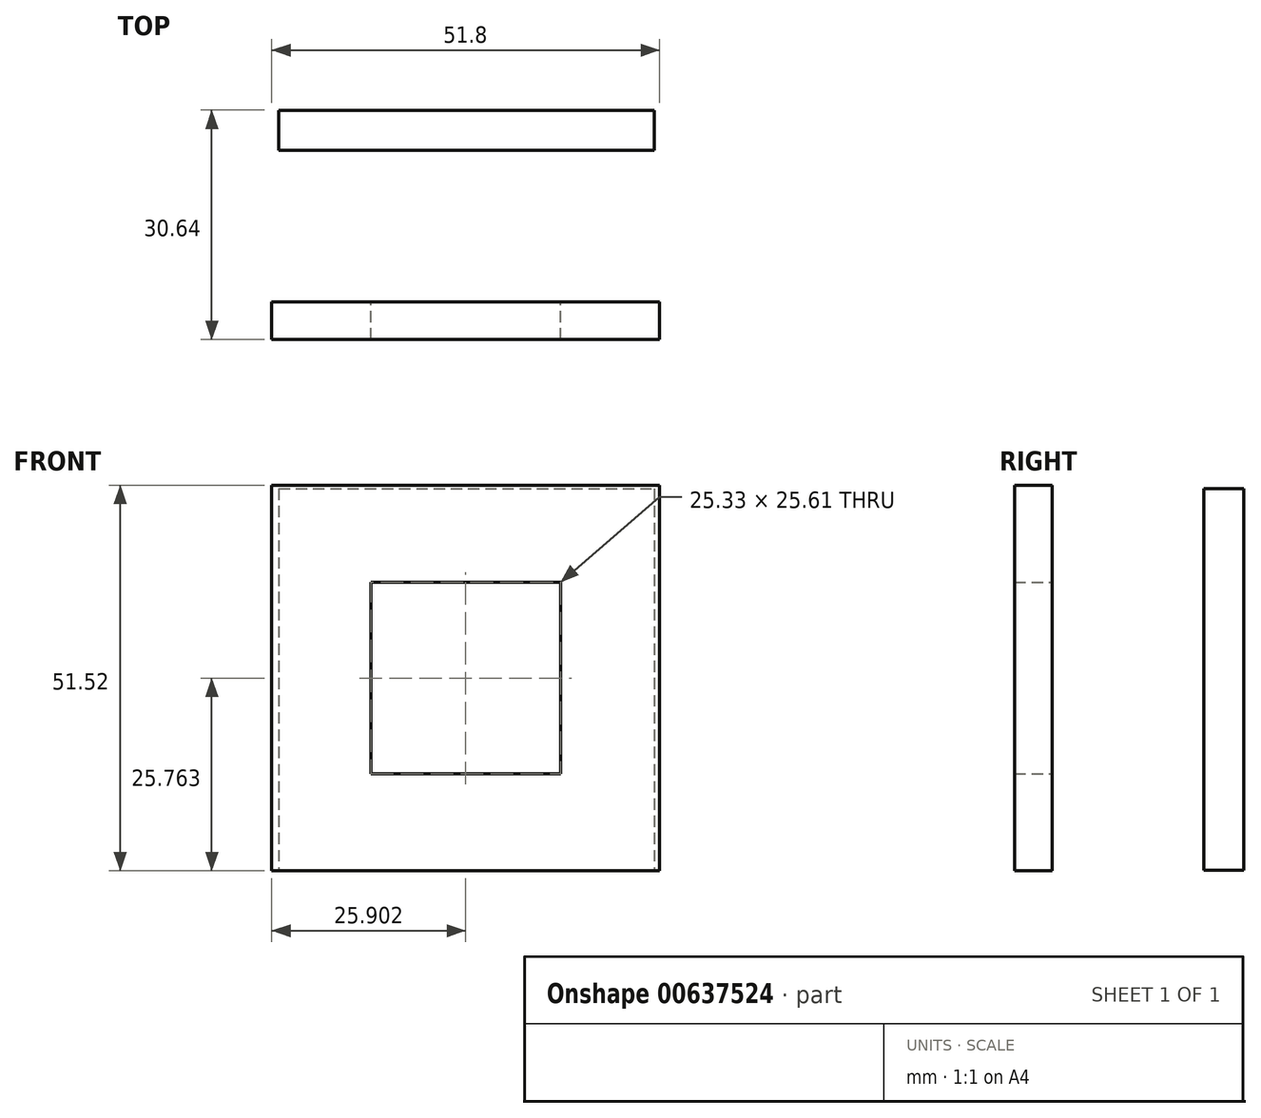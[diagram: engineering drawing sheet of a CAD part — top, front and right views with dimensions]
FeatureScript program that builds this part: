
annotation { "Feature Type Name" : "Feature", "Feature Type Description" : "" }
export const myFeature = defineFeature(function(context is Context, id is Id, definition is map)
    precondition{}
    {
        {
            var Q0;
            Q0=qCreatedBy(makeId("Front.planeOp"),FACE);
            var sketch = newSketch(context, id + "F0", { "sketchPlane" : qUnion([Q0])});
            skLineSegment(sketch, "E0.bottom", {"start": v(-22.88, 21.44) * mm, "end": v(28.92, 21.44) * mm});
            skLineSegment(sketch, "E0.top", {"start": v(-22.88, -30.08) * mm, "end": v(28.92, -30.08) * mm});
            skLineSegment(sketch, "E0.left", {"start": v(-22.88, 21.44) * mm, "end": v(-22.88, -30.08) * mm});
            skLineSegment(sketch, "E0.right", {"start": v(28.92, 21.44) * mm, "end": v(28.92, -30.08) * mm});
            skLineSegment(sketch, "E1.bottom", {"start": v(-9.64, 8.5) * mm, "end": v(15.69, 8.5) * mm});
            skLineSegment(sketch, "E1.top", {"start": v(-9.64, -17.12) * mm, "end": v(15.69, -17.12) * mm});
            skLineSegment(sketch, "E1.left", {"start": v(-9.64, 8.5) * mm, "end": v(-9.64, -17.12) * mm});
            skLineSegment(sketch, "E1.right", {"start": v(15.69, 8.5) * mm, "end": v(15.69, -17.12) * mm});
            skSolve(sketch);
        }
        {
            var Q0;
            Q0=makeQuery(id+"F0.imprint","IMPRINT",FACE,{"disambiguationData":[TD([[makeQuery(id+"F0.imprint","IMPRINT",EDGE,{"derivedFrom":sQuery(id+"F0.wireOp",EDGE,"E0.bottom")}),-1.0]])]});
            extrude(context, id + "F1", {"entities" : qUnion([Q0]), "depth" : 5 * mm, "offsetDistance" : 25.4 * mm});
        }
        {
            var Q0;
            Q0=sQuery(id+"F0.wireOp",EDGE,"E1.right");
            var Q1;
            Q1=sQuery(id+"F0.wireOp",EDGE,"E1.bottom");
            var Q2;
            Q2=sQuery(id+"F0.wireOp",EDGE,"E1.left");
            var Q3;
            Q3=sQuery(id+"F0.wireOp",EDGE,"E1.top");
            extrude(context, id + "F2", {"bodyType" : ToolBodyType.SURFACE, "surfaceEntities" : qUnion([Q0, Q1, Q2, Q3]), "oppositeDirection" : true, "depth" : 20 * mm, "offsetDistance" : 25 * mm});
        }
        {
            var Q0;
            Q0=qCreatedBy(makeId("Top.planeOp"),FACE);
            var sketch = newSketch(context, id + "F3", { "sketchPlane" : qUnion([Q0])});
            skLineSegment(sketch, "E2.bottom", {"start": v(-21.95, 20.25) * mm, "end": v(28.19, 20.25) * mm});
            skLineSegment(sketch, "E2.top", {"start": v(-21.95, 25.64) * mm, "end": v(28.19, 25.64) * mm});
            skLineSegment(sketch, "E2.left", {"start": v(-21.95, 20.25) * mm, "end": v(-21.95, 25.64) * mm});
            skLineSegment(sketch, "E2.right", {"start": v(28.19, 20.25) * mm, "end": v(28.19, 25.64) * mm});
            skSolve(sketch);
        }
        {
            var Q0;
            Q0=makeQuery(id+"F3.imprint","IMPRINT",FACE,{"disambiguationData":[TD([[makeQuery(id+"F3.imprint","IMPRINT",EDGE,{"derivedFrom":sQuery(id+"F3.wireOp",EDGE,"E2.bottom")}),1.0]])]});
            extrude(context, id + "F4", {"entities" : qUnion([Q0]), "depth" : 21 * mm, "offsetDistance" : 25 * mm});
        }
        {
            var Q0;
            Q0=makeQuery(id+"F4.opExtrude","CAP_FACE",FACE,{"disambiguationData":[OSD([sQuery(id+"F3.wireOp",EDGE,"E2.bottom"),sQuery(id+"F3.wireOp",EDGE,"E2.top"),sQuery(id+"F3.wireOp",EDGE,"E2.left"),sQuery(id+"F3.wireOp",EDGE,"E2.right")])],"isStart":true});
            extrude(context, id + "F5", {"entities" : qUnion([Q0]), "operationType" : NewBodyOperationType.ADD, "depth" : 30 * mm, "offsetDistance" : 25 * mm});
        }
    });
